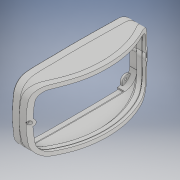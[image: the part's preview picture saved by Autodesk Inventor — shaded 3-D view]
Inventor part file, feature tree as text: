
AUTODESK INVENTOR PART (.ipt)
format: ipt  version: 2019 (Build 230136000, 136)  size: 3,369,472 bytes
history: native  units: mm
features: extrude x14, sketch x10, projected_geometry x6, hole x3, plane x3, other x3, fillet x1
ambient origin geometry x8: Origin, YZ Plane, XZ Plane, XY Plane, X Axis, Y Axis, Z Axis, Center Point
bodies: Volumenkörper7 (feature_tree), Volumenkörper8 (feature_tree), Volumenkörper9 (feature_tree), Volumenkörper11 (feature_tree)
feature tree (40):
  sketch  "Skizze1"  dims[d8=1.000002mm d10=3.000002mm]
  extrude  "Extrusion3"  Depth=3.000002mm
  extrude  "Extrusion4"  Depth=10.0mm TaperAngle=0.0deg
  sketch  "Skizze2"  dims[d11=1.2mm d12=0.0mm d13=10.0mm d14=0.0mm]
  extrude  "Extrusion5"  Depth=8.0mm
  sketch  "Skizze3"  dims[d16=8.0mm d17=8.0mm]
  hole  "Bohrung1"  [1 undecoded]
  extrude  "Extrusion7"  Depth=138.0mm
  plane  "Arbeitsebene1"
  plane  "Arbeitsebene2"
  extrude  "Extrusion14"  Depth=10.0mm TaperAngle=0.0deg
  sketch  "Skizze7"  dims[d20=3.0mm d21=0.0mm]
  extrude  "Extrusion11"  Depth=140.0mm
  extrude  "Extrusion15"  Depth=3.0mm
  extrude  "Extrusion13"  Depth=6.0mm
  extrude  "Extrusion16"  Depth=40.0mm TaperAngle=0.0deg
  extrude  "Extrusion17"  Depth=3.000001mm
  extrude  "Extrusion20"  Depth=40.0mm TaperAngle=0.0deg
  extrude  "Extrusion21"  Depth=50.0mm TaperAngle=0.0deg
  other  "Kombinieren1"
  extrude  "Extrusion22"  Depth=40.0mm TaperAngle=0.0deg
  other  "Kombinieren2"
  fillet  "Rundung1"  Radius=0.499998mm
  plane  "Arbeitsebene4"
  sketch  "Skizze17"  dims[d49=3.0mm d50=3.0mm]
  hole  "Bohrung3"  [1 undecoded]
  hole  "Bohrung4"  [1 undecoded]
  extrude  "Extrusion25"  Depth=5.0mm
  other  "Bild1"
  projected_geometry  "Projizierte Kontur1"
  sketch  "Skizze6"  dims[d18=8.0mm d19=8.0mm]
  projected_geometry  "Projizierte Kontur3"
  sketch  "Skizze9"  dims[d26=3.5mm d27=6.0mm d28=4.0mm d29=2.0mm d30=90.0deg d31=8.0mm d32=20.594885mm d33=138.0mm]
  projected_geometry  "Projizierte Kontur4"
  sketch  "Skizze10"  dims[d34=138.0mm d35=10.0mm d36=0.0mm]
  projected_geometry  "Projizierte Kontur5"
  sketch  "Skizze12"  dims[d43=40.0mm d44=0.0mm d45=140.0mm]
  projected_geometry  "Projizierte Kontur7"
  projected_geometry  "Projizierte Kontur10"
  sketch  "Skizze18"  dims[d51=40.0mm d52=0.0mm d53=6.0mm d54=40.0mm d55=0.0mm d56=3.000001mm d57=40.0mm d58=0.0mm d59=50.0mm d60=0.0mm d61=40.0mm d62=0.0mm d63=0.499998mm d69=50.0mm d70=0.0mm d71=40.0mm d72=0.0mm d73=5.0mm d74=40.0mm d75=0.0mm d76=0.75mm d77=3.0mm d95=50.0mm d96=6.0mm d97=6.0mm d98=3.0mm d99=6.0mm d100=4.0mm d101=2.0mm d102=90.0deg d103=8.0mm d104=20.594885mm d105=5.5mm d106=6.0mm d107=4.0mm d108=2.0mm d109=90.0deg d110=30.0mm d111=0.0mm d112=40.0mm d113=0.0mm]
note: 3 required parameter values undecoded (feature->parameter linkage not recoverable at this tier; creation-order binding heuristic only, values carry confidence <= 0.55)
